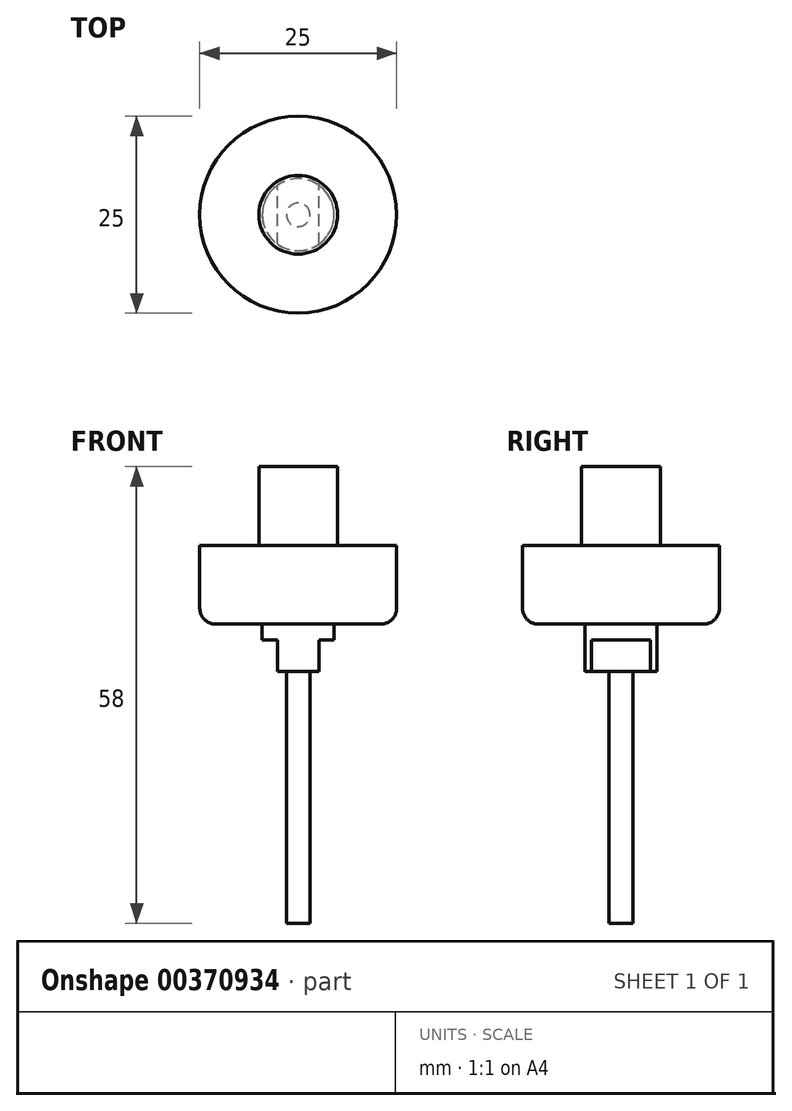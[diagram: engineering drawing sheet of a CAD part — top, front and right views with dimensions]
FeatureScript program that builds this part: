
annotation { "Feature Type Name" : "Feature", "Feature Type Description" : "" }
export const myFeature = defineFeature(function(context is Context, id is Id, definition is map)
    precondition{}
    {
        {
            var Q0;
            Q0=qCreatedBy(makeId("Top.planeOp"),FACE);
            var sketch = newSketch(context, id + "F0", { "sketchPlane" : qUnion([Q0])});
            skCircle(sketch, "E0", {"center": v(0, 0) * mm, "radius": 12.5 * mm});
            skSolve(sketch);
        }
        {
            var Q0;
            Q0=makeQuery(id+"F0.imprint","IMPRINT",FACE,{"disambiguationData":[TD([[makeQuery(id+"F0.imprint","IMPRINT",EDGE,{"derivedFrom":sQuery(id+"F0.wireOp",EDGE,"E0")}),1.0]])]});
            extrude(context, id + "F1", {"entities" : qUnion([Q0]), "depth" : 10 * mm});
        }
        {
            var Q0;
            Q0=makeQuery(id+"F1.opExtrude","CAP_FACE",FACE,{"disambiguationData":[OSD([sQuery(id+"F0.wireOp",EDGE,"E0")])],"isStart":false});
            var sketch = newSketch(context, id + "F2", { "sketchPlane" : qUnion([Q0])});
            skCircle(sketch, "E1", {"center": v(0, 0) * mm, "radius": 5 * mm});
            skSolve(sketch);
        }
        {
            var Q0;
            Q0=makeQuery(id+"F2.imprint","IMPRINT",FACE,{"disambiguationData":[TD([[makeQuery(id+"F2.imprint","IMPRINT",EDGE,{"derivedFrom":sQuery(id+"F2.wireOp",EDGE,"E1")}),1.0]])]});
            extrude(context, id + "F3", {"entities" : qUnion([Q0]), "operationType" : NewBodyOperationType.ADD, "depth" : 10 * mm});
        }
        {
            var Q0;
            Q0=makeQuery(id+"F1.opExtrude","CAP_FACE",FACE,{"disambiguationData":[OSD([sQuery(id+"F0.wireOp",EDGE,"E0")])],"isStart":true});
            var sketch = newSketch(context, id + "F4", { "sketchPlane" : qUnion([Q0])});
            skCircle(sketch, "E2", {"center": v(0, 0) * mm, "radius": 4.57 * mm});
            skSolve(sketch);
        }
        {
            var Q0;
            Q0=makeQuery(id+"F4.imprint","IMPRINT",FACE,{"disambiguationData":[TD([[makeQuery(id+"F4.imprint","IMPRINT",EDGE,{"derivedFrom":sQuery(id+"F4.wireOp",EDGE,"E2")}),1.0]])]});
            extrude(context, id + "F5", {"entities" : qUnion([Q0]), "operationType" : NewBodyOperationType.ADD, "depth" : 6 * mm});
        }
        {
            var Q0;
            Q0=makeQuery(id+"F5.opExtrude","CAP_FACE",FACE,{"disambiguationData":[OSD([sQuery(id+"F4.wireOp",EDGE,"E2")])],"isStart":false});
            var sketch = newSketch(context, id + "F6", { "sketchPlane" : qUnion([Q0])});
            skCircle(sketch, "E3", {"center": v(0, 0) * mm, "radius": 1.5 * mm});
            skSolve(sketch);
        }
        {
            var Q0;
            Q0=makeQuery(id+"F6.imprint","IMPRINT",FACE,{"disambiguationData":[TD([[makeQuery(id+"F6.imprint","IMPRINT",EDGE,{"derivedFrom":sQuery(id+"F6.wireOp",EDGE,"E3")}),1.0]])]});
            extrude(context, id + "F7", {"entities" : qUnion([Q0]), "operationType" : NewBodyOperationType.ADD, "depth" : 32 * mm});
        }
        {
            var Q0;
            Q0=makeQuery(id+"F1.opExtrude","CAP_EDGE",EDGE,{"disambiguationData":[OSD([sQuery(id+"F0.wireOp",EDGE,"E0")])],"isStart":true});
            fillet(context, id + "F8", {"entities" : qUnion([Q0]), "radius" : 2 * mm, "tangentPropagation" : true, "allowEdgeOverflow" : false});
        }
        {
            var Q0;
            Q0=makeQuery(id+"F5.opExtrude","CAP_FACE",FACE,{"disambiguationData":[OSD([sQuery(id+"F4.wireOp",EDGE,"E2")])],"isStart":false});
            var sketch = newSketch(context, id + "F9", { "sketchPlane" : qUnion([Q0])});
            skLineSegment(sketch, "E4", {"start": v(2.62, 3.75) * mm, "end": v(2.62, -3.75) * mm});
            skLineSegment(sketch, "E5", {"start": v(-2.62, 3.75) * mm, "end": v(-2.62, -3.75) * mm});
            skCircle(sketch, "E6", {"center": v(0, 0) * mm, "radius": 4.57 * mm});
            skSolve(sketch);
        }
        {
            var Q0;
            {var subQ0=sQuery(id+"F9.wireOp",EDGE,"E4");Q0=makeQuery(id+"F9.imprint","IMPRINT",FACE,{"disambiguationData":[TD([[makeQuery(id+"F9.imprint","IMPRINT",EDGE,{"derivedFrom":subQ0}),1.0]])]});}
            var Q1;
            {var subQ0=sQuery(id+"F9.wireOp",EDGE,"E5");Q1=makeQuery(id+"F9.imprint","IMPRINT",FACE,{"disambiguationData":[TD([[makeQuery(id+"F9.imprint","IMPRINT",EDGE,{"derivedFrom":subQ0}),-1.0]])]});}
            extrude(context, id + "F10", {"entities" : qUnion([Q0, Q1]), "operationType" : NewBodyOperationType.REMOVE, "oppositeDirection" : true, "depth" : 4 * mm});
        }
    });
